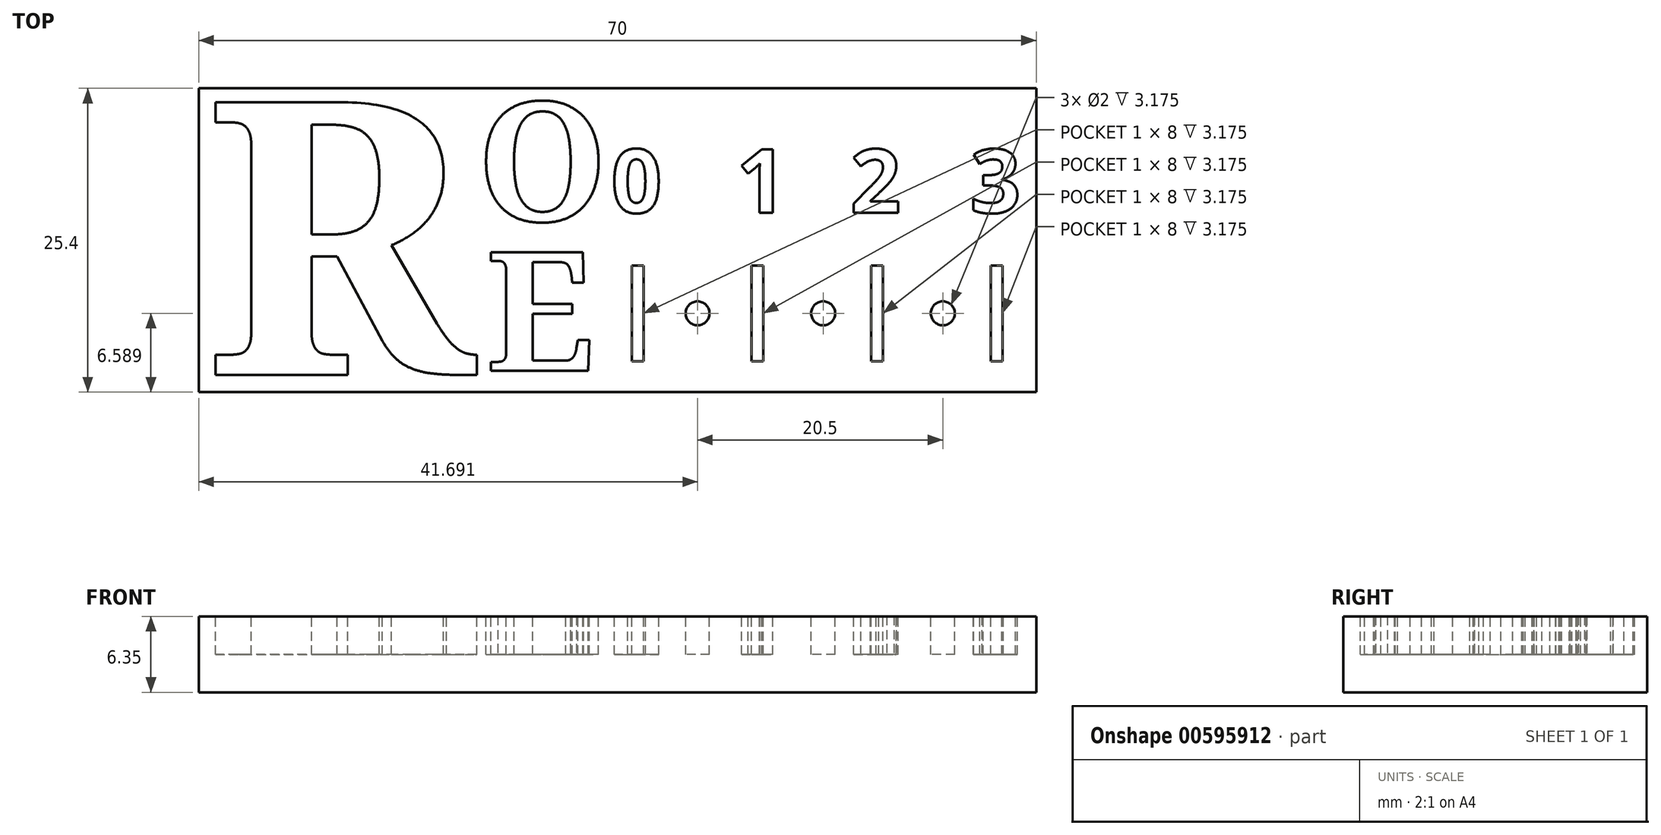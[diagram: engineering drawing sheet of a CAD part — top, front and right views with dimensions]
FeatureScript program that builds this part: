
annotation { "Feature Type Name" : "Feature", "Feature Type Description" : "" }
export const myFeature = defineFeature(function(context is Context, id is Id, definition is map)
    precondition{}
    {
        {
            var Q0;
            Q0=qCreatedBy(makeId("Top.planeOp"),FACE);
            var sketch = newSketch(context, id + "F0", { "sketchPlane" : qUnion([Q0])});
            skLineSegment(sketch, "E0.bottom", {"start": v(-59.27, 9.73) * mm, "end": v(10.73, 9.73) * mm});
            skLineSegment(sketch, "E0.top", {"start": v(-59.27, -15.67) * mm, "end": v(10.73, -15.67) * mm});
            skLineSegment(sketch, "E0.left", {"start": v(-59.27, 9.73) * mm, "end": v(-59.27, -15.67) * mm});
            skLineSegment(sketch, "E0.right", {"start": v(10.73, 9.73) * mm, "end": v(10.73, -15.67) * mm});
            skSolve(sketch);
        }
        {
            var Q0;
            Q0=qSketchRegion(id+"F0",true);
            extrude(context, id + "F1", {"entities" : qUnion([Q0]), "depth" : 6.35 * mm, "offsetDistance" : 25.4 * mm});
        }
        {
            var Q0;
            Q0=makeQuery(id+"F1.opExtrude","CAP_FACE",FACE,{"disambiguationData":[OSD([sQuery(id+"F0.wireOp",EDGE,"E0.bottom"),sQuery(id+"F0.wireOp",EDGE,"E0.top"),sQuery(id+"F0.wireOp",EDGE,"E0.left"),sQuery(id+"F0.wireOp",EDGE,"E0.right")])],"isStart":false});
            var sketch = newSketch(context, id + "F2", { "sketchPlane" : qUnion([Q0])});
            skText(sketch, "E1", { "text": "R", "fontName": "NotoSerif-Bold.ttf"});
            skText(sketch, "E2", { "text": "O\n", "fontName": "NotoSerif-Bold.ttf"});
            skText(sketch, "E3", { "text": "E", "fontName": "NotoSerif-Bold.ttf"});
            skLineSegment(sketch, "E4.bottom", {"start": v(-23.08, -5.08) * mm, "end": v(-22.08, -5.08) * mm});
            skLineSegment(sketch, "E4.top", {"start": v(-23.08, -13.08) * mm, "end": v(-22.08, -13.08) * mm});
            skLineSegment(sketch, "E4.left", {"start": v(-23.08, -5.08) * mm, "end": v(-23.08, -13.08) * mm});
            skLineSegment(sketch, "E4.right", {"start": v(-22.08, -5.08) * mm, "end": v(-22.08, -13.08) * mm});
            skLineSegment(sketch, "E5.bottom", {"start": v(-13.08, -5.08) * mm, "end": v(-12.08, -5.08) * mm});
            skLineSegment(sketch, "E5.top", {"start": v(-13.08, -13.08) * mm, "end": v(-12.08, -13.08) * mm});
            skLineSegment(sketch, "E5.left", {"start": v(-13.08, -5.08) * mm, "end": v(-13.08, -13.08) * mm});
            skLineSegment(sketch, "E5.right", {"start": v(-12.08, -5.08) * mm, "end": v(-12.08, -13.08) * mm});
            skLineSegment(sketch, "E6.bottom", {"start": v(-3.08, -5.08) * mm, "end": v(-2.08, -5.08) * mm});
            skLineSegment(sketch, "E6.top", {"start": v(-3.08, -13.08) * mm, "end": v(-2.08, -13.08) * mm});
            skLineSegment(sketch, "E6.left", {"start": v(-3.08, -5.08) * mm, "end": v(-3.08, -13.08) * mm});
            skLineSegment(sketch, "E6.right", {"start": v(-2.08, -5.08) * mm, "end": v(-2.08, -13.08) * mm});
            skLineSegment(sketch, "E7.bottom", {"start": v(6.92, -5.08) * mm, "end": v(7.92, -5.08) * mm});
            skLineSegment(sketch, "E7.top", {"start": v(6.92, -13.08) * mm, "end": v(7.92, -13.08) * mm});
            skLineSegment(sketch, "E7.left", {"start": v(6.92, -5.08) * mm, "end": v(6.92, -13.08) * mm});
            skLineSegment(sketch, "E7.right", {"start": v(7.92, -5.08) * mm, "end": v(7.92, -13.08) * mm});
            skPoint(sketch, "E8", {"position": v(-22.58, -5.08) * mm});
            skPoint(sketch, "E9", {"position": v(-12.58, -5.08) * mm});
            skPoint(sketch, "E10", {"position": v(-2.58, -5.08) * mm});
            skCircle(sketch, "E11", {"center": v(-17.58, -9.08) * mm, "radius": 1 * mm});
            skPoint(sketch, "E12", {"position": v(-22.08, -9.08) * mm});
            skCircle(sketch, "E13", {"center": v(-7.08, -9.08) * mm, "radius": 1 * mm});
            skCircle(sketch, "E14", {"center": v(2.92, -9.08) * mm, "radius": 1 * mm});
            skPoint(sketch, "E15", {"position": v(-12.08, -9.08) * mm});
            skPoint(sketch, "E16", {"position": v(-2.08, -9.08) * mm});
            skText(sketch, "E17", { "text": "0", "fontName": "OpenSans-Bold.ttf"});
            skText(sketch, "E18", { "text": "1", "fontName": "OpenSans-Bold.ttf"});
            skText(sketch, "E19", { "text": "2", "fontName": "OpenSans-Bold.ttf"});
            skText(sketch, "E20", { "text": "3", "fontName": "OpenSans-Bold.ttf"});
            const initialGuessF2  = {"E1": [-0.05875, -0.01424, 1, 0, 0.023], "E2": [-0.03602, -0.00137, 1, 0, 0.01], "E3": [-0.03525, -0.01388, 1, 0, 0.01], "E17": [-0.0248, -0.00068, 1, 0, 0.00534], "E18": [-0.01435, -0.00068, 1, 0, 0.00534], "E19": [-0.00482, -0.00068, 1, 0, 0.00534], "E20": [0.0052, -0.00068, 1, 0, 0.00534]};
            skSetInitialGuess(sketch, initialGuessF2);
            skSolve(sketch);
        }
        {
            var Q0;
            Q0=qSketchRegion(id+"F2",true);
            extrude(context, id + "F3", {"entities" : qUnion([Q0]), "operationType" : NewBodyOperationType.REMOVE, "oppositeDirection" : true, "depth" : 3.17 * mm, "offsetDistance" : 25.4 * mm});
        }
    });
